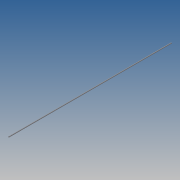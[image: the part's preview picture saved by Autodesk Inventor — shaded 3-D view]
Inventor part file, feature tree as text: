
AUTODESK INVENTOR PART (.ipt)
format: ipt  version: 2014 SP1 (Build 180222100, 222)  size: 74,240 bytes
history: native  units: in
note: dims shown in document units (in); Inventor stores cm internally (conversion verified against a paired STEP export)
features: extrude x1, sketch x1
ambient origin geometry x8: Origin, YZ Plane, XZ Plane, XY Plane, X Axis, Y Axis, Z Axis, Center Point
bodies: Solid1 (feature_tree)
feature tree (2):
  extrude  "Extrusion1"  Depth=787.4016in
  sketch  "Sketch1"  dims[d0=3.937in d1=0.175in d2=787.4016in d3=0.0in]
